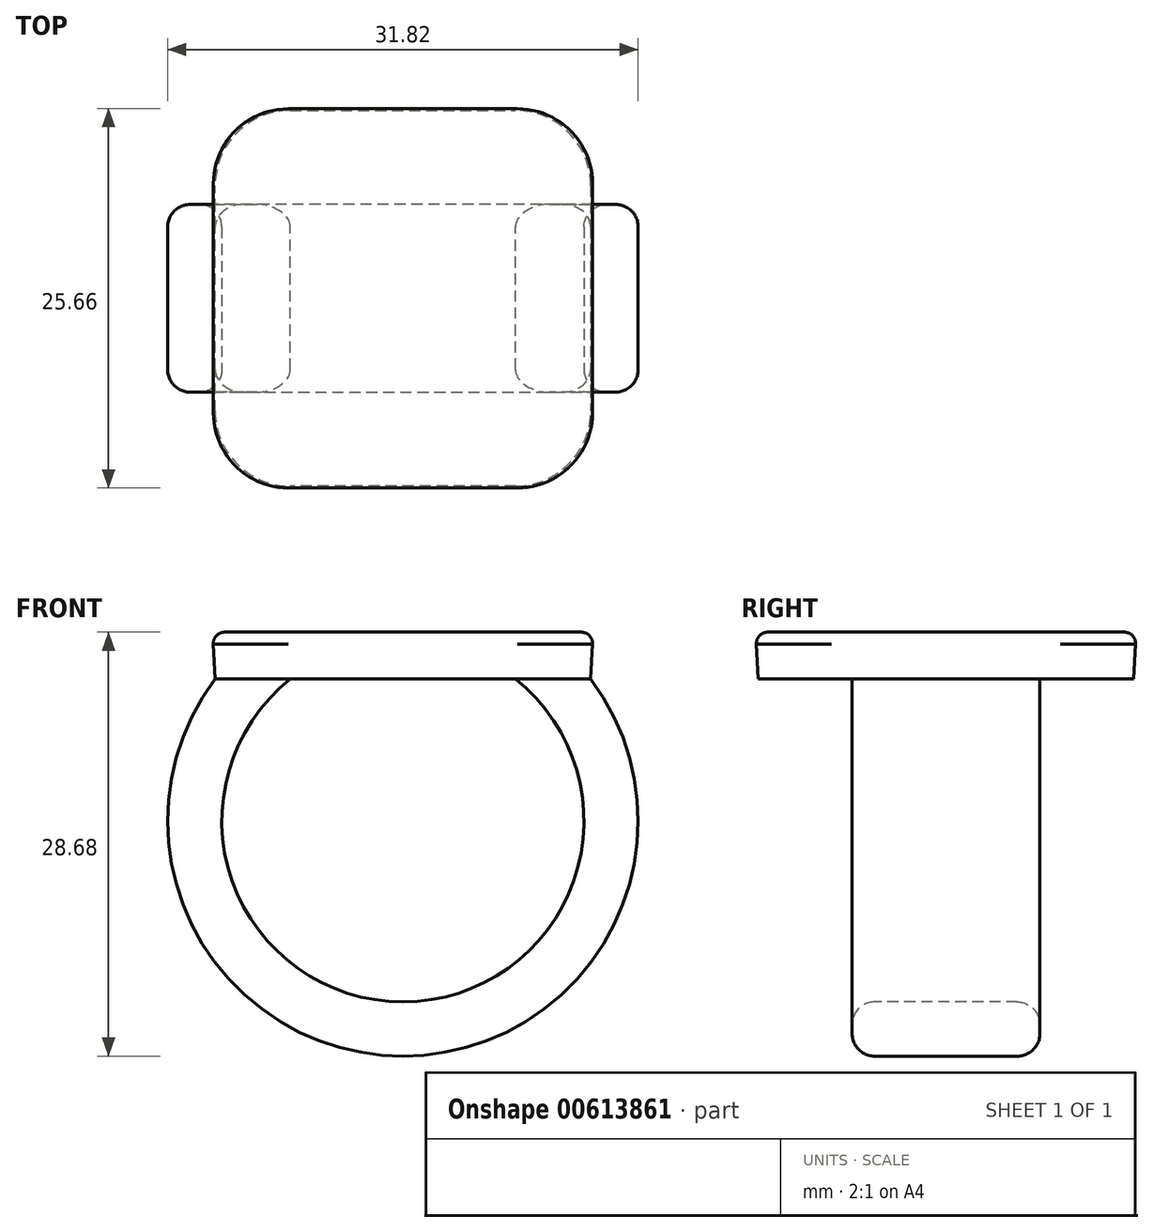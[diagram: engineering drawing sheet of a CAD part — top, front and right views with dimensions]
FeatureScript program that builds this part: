
annotation { "Feature Type Name" : "Feature", "Feature Type Description" : "" }
export const myFeature = defineFeature(function(context is Context, id is Id, definition is map)
    precondition{}
    {
        {
            var Q0;
            Q0=qCreatedBy(makeId("Top.planeOp"),FACE);
            var sketch = newSketch(context, id + "F0", { "sketchPlane" : qUnion([Q0])});
            skLineSegment(sketch, "E0.bottom", {"start": v(-12.7, 12.7) * mm, "end": v(12.7, 12.7) * mm});
            skLineSegment(sketch, "E0.top", {"start": v(-12.7, -12.7) * mm, "end": v(12.7, -12.7) * mm});
            skLineSegment(sketch, "E0.left", {"start": v(-12.7, 12.7) * mm, "end": v(-12.7, -12.7) * mm});
            skLineSegment(sketch, "E0.right", {"start": v(12.7, 12.7) * mm, "end": v(12.7, -12.7) * mm});
            skPoint(sketch, "E0.middle", {"position": v(0, 0) * mm});
            skSolve(sketch);
        }
        {
            var Q0;
            Q0=makeQuery(id+"F0.imprint","IMPRINT",FACE,{"disambiguationData":[TD([[makeQuery(id+"F0.imprint","IMPRINT",EDGE,{"derivedFrom":sQuery(id+"F0.wireOp",EDGE,"E0.bottom")}),-1.0]])]});
            extrude(context, id + "F1", {"entities" : qUnion([Q0]), "depth" : 3.17 * mm, "offsetDistance" : 25.4 * mm, "hasDraft" : true, "draftAngle" : 3 * degree});
        }
        {
            var Q0;
            Q0=qCreatedBy(makeId("Front.planeOp"),FACE);
            var sketch = newSketch(context, id + "F2", { "sketchPlane" : qUnion([Q0])});
            skArc(sketch, "E1", {"start": v(-10.16, 0) * mm, "mid": v(0, -23.56) * mm, "end": v(10.16, 0) * mm});
            skSolve(sketch);
        }
        {
            var Q0;
            Q0=makeQuery(id+"F1.opExtrude","CAP_FACE",FACE,{"disambiguationData":[OSD([sQuery(id+"F0.wireOp",EDGE,"E0.bottom"),sQuery(id+"F0.wireOp",EDGE,"E0.top"),sQuery(id+"F0.wireOp",EDGE,"E0.left"),sQuery(id+"F0.wireOp",EDGE,"E0.right")])],"isStart":true});
            var sketch = newSketch(context, id + "F3", { "sketchPlane" : qUnion([Q0])});
            skLineSegment(sketch, "E2.bottom", {"start": v(-12.7, 6.35) * mm, "end": v(-7.62, 6.35) * mm});
            skLineSegment(sketch, "E2.top", {"start": v(-12.7, -6.35) * mm, "end": v(-7.62, -6.35) * mm});
            skLineSegment(sketch, "E2.left", {"start": v(-12.7, 6.35) * mm, "end": v(-12.7, -6.35) * mm});
            skLineSegment(sketch, "E2.right", {"start": v(-7.62, 6.35) * mm, "end": v(-7.62, -6.35) * mm});
            skPoint(sketch, "E2.middle", {"position": v(-10.16, 0) * mm});
            skSolve(sketch);
        }
        {
            var Q0;
            Q0 = qSketchRegion(id + "F3", true);
            var Q1;
            Q1 = qConstructionFilter(qBodyType(qCreatedBy(id + "F2" ,EDGE), BodyType.WIRE), ConstructionObject.NO);
            sweep(context, id + "F4", {"operationType" : NewBodyOperationType.ADD, "profiles" : qUnion([Q0]), "path" : qUnion([Q1])});
        }
        {
            var Q0;
            Q0=qCreatedBy(makeId("Front.planeOp"),FACE);
            var sketch = newSketch(context, id + "F5", { "sketchPlane" : qUnion([Q0])});
            skArc(sketch, "E3.1", {"start": v(-7.62, 0) * mm, "mid": v(0, -21.84) * mm, "end": v(7.62, 0) * mm});
            skLineSegment(sketch, "E3.2", {"start": v(10.01, -2.54) * mm, "end": v(10.16, 0) * mm});
            skLineSegment(sketch, "E4.trimOffspring", {"start": v(7.62, 0) * mm, "end": v(10.16, 0) * mm});
            skPoint(sketch, "E3.0.start.orphan", {"position": v(-12.7, 0) * mm});
            skPoint(sketch, "E5.orphan", {"position": v(12.7, 0) * mm});
            skSolve(sketch);
        }
        {
            var Q0;
            {var subQ2=sQuery(id+"F5.wireOp",EDGE,"E3.2");Q0=makeQuery(id+"F5.imprint","IMPRINT",FACE,{"disambiguationData":[TD([[makeQuery(id+"F5.imprint","IMPRINT",EDGE,{"derivedFrom":subQ2}),1.0]])]});}
            var Q1;
            Q1=makeQuery(id+"F4.opSweep","SWEPT_FACE",FACE,{"disambiguationData":[OSD([sQuery(id+"F2.wireOp",EDGE,"E1"),sQuery(id+"F3.wireOp",EDGE,"E2.bottom")])]});
            var Q2;
            Q2=makeQuery(id+"F4.opSweep","SWEPT_FACE",FACE,{"disambiguationData":[OSD([sQuery(id+"F2.wireOp",EDGE,"E1"),sQuery(id+"F3.wireOp",EDGE,"E2.top")])]});
            extrude(context, id + "F6", {"entities" : qUnion([Q0]), "operationType" : NewBodyOperationType.ADD, "endBound" : BoundingType.UP_TO_SURFACE, "depth" : 25.4 * mm, "endBoundEntityFace" : qUnion([Q1]), "offsetDistance" : 25.4 * mm, "hasSecondDirection" : true, "secondDirectionBound" : SecondDirectionBoundingType.UP_TO_SURFACE, "secondDirectionOppositeDirection" : true, "secondDirectionDepth" : 25.4 * mm, "secondDirectionBoundEntityFace" : qUnion([Q2])});
        }
        {
            var Q0;
            Q0=makeQuery(id+"F1.opExtrude","SWEPT_EDGE",EDGE,{"disambiguationData":[OSD([sQuery(id+"F0.wireOp",EDGE,"E0.top"),sQuery(id+"F0.wireOp",EDGE,"E0.left")])]});
            var Q1;
            Q1=makeQuery(id+"F1.opExtrude","SWEPT_EDGE",EDGE,{"disambiguationData":[OSD([sQuery(id+"F0.wireOp",EDGE,"E0.bottom"),sQuery(id+"F0.wireOp",EDGE,"E0.left")])]});
            var Q2;
            Q2=makeQuery(id+"F1.opExtrude","SWEPT_EDGE",EDGE,{"disambiguationData":[OSD([sQuery(id+"F0.wireOp",EDGE,"E0.bottom"),sQuery(id+"F0.wireOp",EDGE,"E0.right")])]});
            var Q3;
            Q3=makeQuery(id+"F1.opExtrude","SWEPT_EDGE",EDGE,{"disambiguationData":[OSD([sQuery(id+"F0.wireOp",EDGE,"E0.top"),sQuery(id+"F0.wireOp",EDGE,"E0.right")])]});
            fillet(context, id + "F7", {"entities" : qUnion([Q0, Q1, Q2, Q3]), "radius" : 5.08 * mm, "tangentPropagation" : true, "allowEdgeOverflow" : false});
        }
        {
            var Q0;
            Q0=makeQuery(id+"F4.opSweep","SWEPT_EDGE",EDGE,{"disambiguationData":[OSD([sQuery(id+"F0.wireOp",EDGE,"E0.left"),sQuery(id+"F2.wireOp",EDGE,"E1"),sQuery(id+"F3.wireOp",EDGE,"E2.bottom"),sQuery(id+"F3.wireOp",EDGE,"E2.left")])]});
            var Q1;
            {var subQ0=sQuery(id+"F5.wireOp",EDGE,"E3.1");var subQ1=sQuery(id+"F3.wireOp",EDGE,"E2.bottom");var subQ2=sQuery(id+"F2.wireOp",EDGE,"E1");Q1=makeQuery(id+"F6.boolean.opBoolean","MERGE",EDGE,{"derivedFrom":[makeQuery(id+"F4.opSweep","SWEPT_EDGE",EDGE,{"disambiguationData":[OSD([subQ2,subQ1,sQuery(id+"F3.wireOp",EDGE,"E2.right")])]}),makeQuery(id+"F6.opExtrude","TWEAK_EDGE",EDGE,{"derivedFrom":[makeQuery(id+"F4.opSweep","SWEPT_FACE",FACE,{"disambiguationData":[OSD([subQ2,subQ1])]}),makeQuery(id+"F5.imprint","IMPRINT",EDGE,{"disambiguationData":[TD([[makeQuery(id+"F5.imprint","INTERSECT",VERTEX,{"derivedFrom":[subQ0,sQuery(id+"F5.wireOp",EDGE,"E4.trimOffspring")]}),1.0]])],"derivedFrom":subQ0})]})]});}
            var Q2;
            Q2=makeQuery(id+"F4.opSweep","SWEPT_EDGE",EDGE,{"disambiguationData":[OSD([sQuery(id+"F0.wireOp",EDGE,"E0.left"),sQuery(id+"F2.wireOp",EDGE,"E1"),sQuery(id+"F3.wireOp",EDGE,"E2.top"),sQuery(id+"F3.wireOp",EDGE,"E2.left")])]});
            var Q3;
            {var subQ0=sQuery(id+"F5.wireOp",EDGE,"E3.1");var subQ1=sQuery(id+"F3.wireOp",EDGE,"E2.top");var subQ2=sQuery(id+"F2.wireOp",EDGE,"E1");Q3=makeQuery(id+"F6.boolean.opBoolean","MERGE",EDGE,{"derivedFrom":[makeQuery(id+"F4.opSweep","SWEPT_EDGE",EDGE,{"disambiguationData":[OSD([subQ2,subQ1,sQuery(id+"F3.wireOp",EDGE,"E2.right")])]}),makeQuery(id+"F6.opExtrude","TWEAK_EDGE",EDGE,{"derivedFrom":[makeQuery(id+"F4.opSweep","SWEPT_FACE",FACE,{"disambiguationData":[OSD([subQ2,subQ1])]}),makeQuery(id+"F5.imprint","IMPRINT",EDGE,{"disambiguationData":[TD([[makeQuery(id+"F5.imprint","INTERSECT",VERTEX,{"derivedFrom":[subQ0,sQuery(id+"F5.wireOp",EDGE,"E4.trimOffspring")]}),1.0]])],"derivedFrom":subQ0})]})]});}
            fillet(context, id + "F8", {"entities" : qUnion([Q0, Q1, Q2, Q3]), "radius" : 1.52 * mm, "tangentPropagation" : true, "allowEdgeOverflow" : false});
        }
        {
            var Q0;
            Q0=makeQuery(id+"F1.opExtrude","CAP_FACE",FACE,{"disambiguationData":[OSD([sQuery(id+"F0.wireOp",EDGE,"E0.bottom"),sQuery(id+"F0.wireOp",EDGE,"E0.top"),sQuery(id+"F0.wireOp",EDGE,"E0.left"),sQuery(id+"F0.wireOp",EDGE,"E0.right")])],"isStart":false});
            fillet(context, id + "F9", {"entities" : qUnion([Q0]), "radius" : 0.76 * mm, "tangentPropagation" : true, "allowEdgeOverflow" : false});
        }
    });
